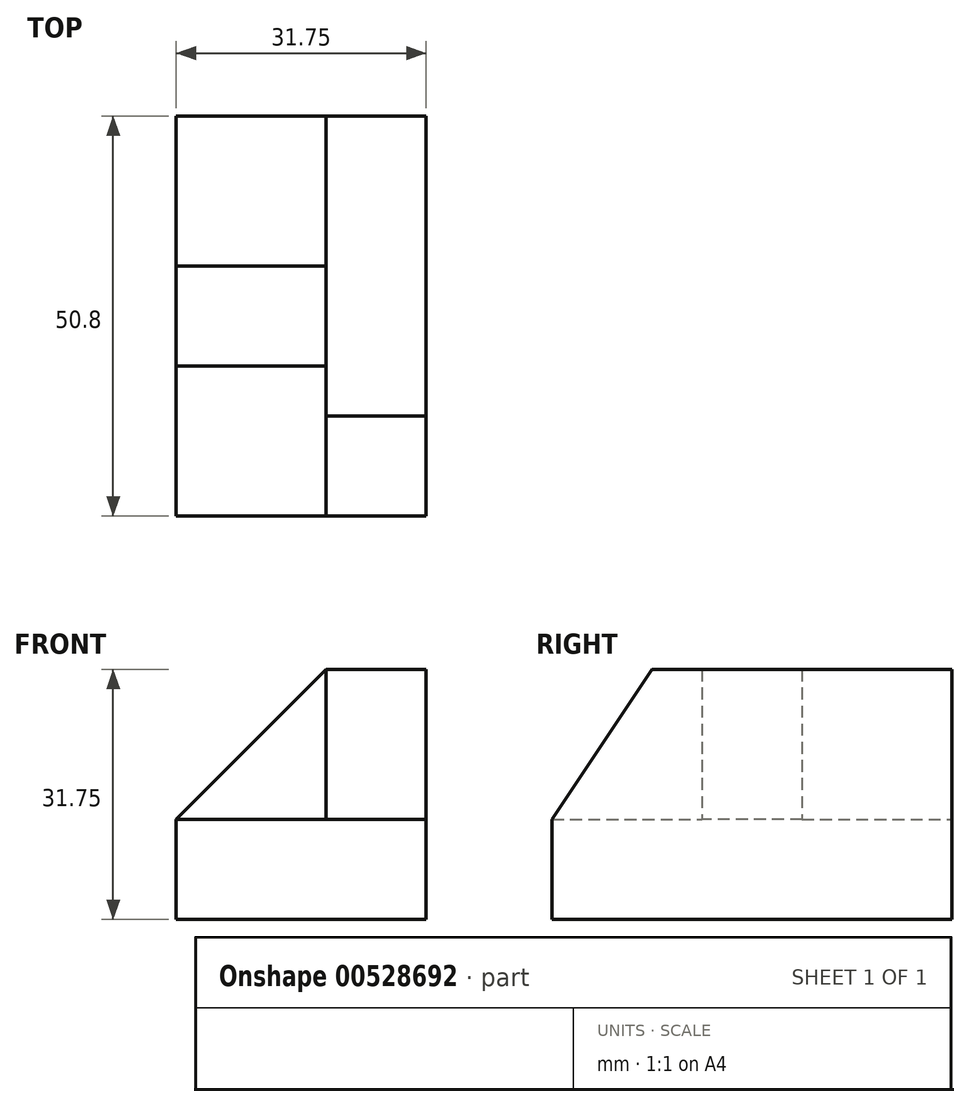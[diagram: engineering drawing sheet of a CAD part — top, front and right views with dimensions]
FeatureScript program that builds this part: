
annotation { "Feature Type Name" : "Feature", "Feature Type Description" : "" }
export const myFeature = defineFeature(function(context is Context, id is Id, definition is map)
    precondition{}
    {
        {
            var Q0;
            Q0=qCreatedBy(makeId("Front.planeOp"),FACE);
            var sketch = newSketch(context, id + "F0", { "sketchPlane" : qUnion([Q0])});
            skLineSegment(sketch, "E0", {"start": v(0, 0) * mm, "end": v(0, 12.7) * mm});
            skLineSegment(sketch, "E1", {"start": v(0, 12.7) * mm, "end": v(19.05, 12.7) * mm});
            skLineSegment(sketch, "E2", {"start": v(19.05, 12.7) * mm, "end": v(19.05, 31.75) * mm});
            skLineSegment(sketch, "E3", {"start": v(19.05, 31.75) * mm, "end": v(31.75, 31.75) * mm});
            skLineSegment(sketch, "E4", {"start": v(31.75, 31.75) * mm, "end": v(31.75, 0) * mm});
            skLineSegment(sketch, "E5", {"start": v(0, 0) * mm, "end": v(31.75, 0) * mm});
            skSolve(sketch);
        }
        {
            var Q0;
            Q0=makeQuery(id+"F0.imprint","IMPRINT",FACE,{"disambiguationData":[TD([[makeQuery(id+"F0.imprint","IMPRINT",EDGE,{"derivedFrom":sQuery(id+"F0.wireOp",EDGE,"E0")}),-1.0]])]});
            extrude(context, id + "F1", {"entities" : qUnion([Q0]), "depth" : 50.8 * mm, "offsetDistance" : 25.4 * mm});
        }
        {
            var Q0;
            Q0=makeQuery(id+"F1.opExtrude","SWEPT_FACE",FACE,{"disambiguationData":[OSD([sQuery(id+"F0.wireOp",EDGE,"E2")])]});
            var sketch = newSketch(context, id + "F2", { "sketchPlane" : qUnion([Q0])});
            skLineSegment(sketch, "E6", {"start": v(19.05, 31.75) * mm, "end": v(19.05, 12.7) * mm});
            skLineSegment(sketch, "E7", {"start": v(31.75, 31.75) * mm, "end": v(31.75, 12.7) * mm});
            skSolve(sketch);
        }
        {
            var Q0;
            {var subQ0=sQuery(id+"F2.wireOp",EDGE,"E6");Q0=makeQuery(id+"F2.imprint","IMPRINT",FACE,{"disambiguationData":[TD([[makeQuery(id+"F2.imprint","IMPRINT",EDGE,{"derivedFrom":subQ0}),1.0]])]});}
            extrude(context, id + "F3", {"entities" : qUnion([Q0]), "operationType" : NewBodyOperationType.ADD, "depth" : 19.05 * mm, "offsetDistance" : 25.4 * mm});
        }
        {
            var Q0;
            Q0=makeQuery(id+"F3.opExtrude","SWEPT_FACE",FACE,{"disambiguationData":[OSD([sQuery(id+"F2.wireOp",EDGE,"E7")])]});
            var sketch = newSketch(context, id + "F4", { "sketchPlane" : qUnion([Q0])});
            skLineSegment(sketch, "E8", {"start": v(0, 12.7) * mm, "end": v(19.05, 31.75) * mm});
            skLineSegment(sketch, "E9", {"start": v(19.05, 31.75) * mm, "end": v(0, 31.75) * mm});
            skLineSegment(sketch, "E10", {"start": v(0, 31.75) * mm, "end": v(0, 12.7) * mm});
            skSolve(sketch);
        }
        {
            var Q0;
            Q0=makeQuery(id+"F4.imprint","IMPRINT",FACE,{"disambiguationData":[TD([[makeQuery(id+"F4.imprint","IMPRINT",EDGE,{"derivedFrom":sQuery(id+"F4.wireOp",EDGE,"E8")}),1.0]])]});
            extrude(context, id + "F5", {"entities" : qUnion([Q0]), "operationType" : NewBodyOperationType.REMOVE, "oppositeDirection" : true, "depth" : 12.7 * mm, "offsetDistance" : 25.4 * mm});
        }
        {
            var Q0;
            {var subQ2=sQuery(id+"F0.wireOp",EDGE,"E2");Q0=makeQuery(id+"F3.boolean.opBoolean","SPLIT",FACE,{"disambiguationData":[TD([makeQuery(id+"F3.opExtrude","SWEPT_FACE",FACE,{"disambiguationData":[OSD([sQuery(id+"F2.wireOp",EDGE,"E7")])]})])],"derivedFrom":makeQuery(id+"F1.opExtrude","SWEPT_FACE",FACE,{"disambiguationData":[OSD([subQ2])]})});}
            var sketch = newSketch(context, id + "F6", { "sketchPlane" : qUnion([Q0])});
            skLineSegment(sketch, "E11", {"start": v(31.75, 31.75) * mm, "end": v(38.1, 31.75) * mm});
            skLineSegment(sketch, "E12", {"start": v(38.1, 31.75) * mm, "end": v(50.8, 12.7) * mm});
            skSolve(sketch);
        }
        {
            var Q0;
            {var subQ0=sQuery(id+"F6.wireOp",EDGE,"E12");Q0=makeQuery(id+"F6.imprint","IMPRINT",FACE,{"disambiguationData":[TD([[makeQuery(id+"F6.imprint","IMPRINT",EDGE,{"derivedFrom":subQ0}),1.0]])]});}
            extrude(context, id + "F7", {"entities" : qUnion([Q0]), "operationType" : NewBodyOperationType.REMOVE, "oppositeDirection" : true, "depth" : 12.7 * mm, "offsetDistance" : 25.4 * mm});
        }
    });
